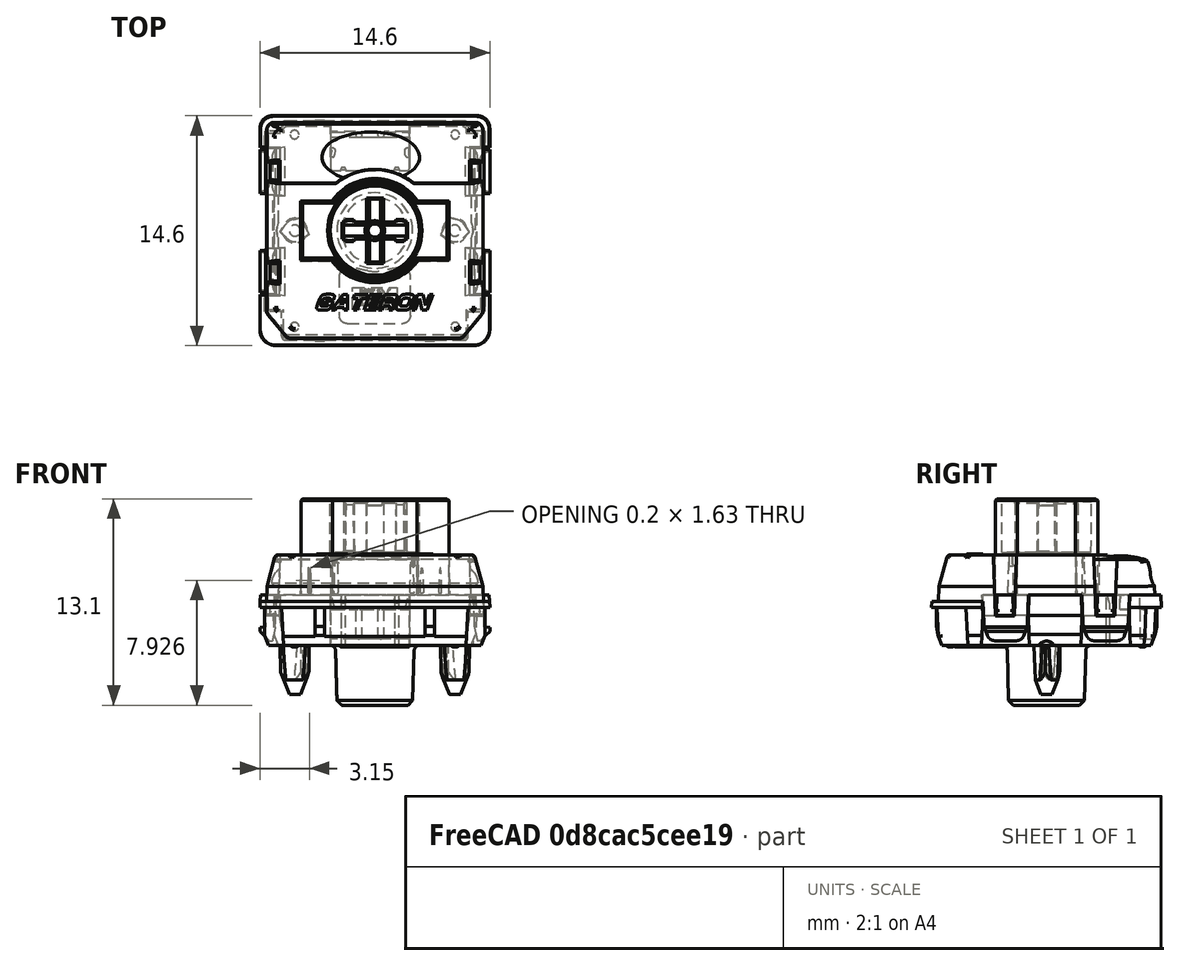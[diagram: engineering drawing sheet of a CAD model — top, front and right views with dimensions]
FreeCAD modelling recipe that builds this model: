
FCSTD DOCUMENT  (FreeCAD 1.0R39319 (Git))
Label: THT-HALL-SWITCH
License: All rights reserved
LicenseURL: https://en.wikipedia.org/wiki/All_rights_reserved
objects: PartDesign::CoordinateSystem×2, Part::Feature×1, PartDesign::FeatureBase×1, PartDesign::Body×1
note: 6 computed .brp shape members not serialized (recipe doc carries the construction recipe); baked Part::Feature solids carry a one-line shape summary decoded from their .brp

FEATURE [Part::Feature] Part__Feature  label="SOLID"
  Placement = pos=(13.3,-4.5,-1.1) rot=(0,0,1;0rad)
  shape: bbox 14.78 x 14.78 x 13.28 mm, 728 faces (baked)
FEATURE [PartDesign::CoordinateSystem] LCS_Origin
  AttacherType = Attacher::AttachEngine3D
  AttachmentOffset = pos=(-13.3,4.5,1.1) rot=(0,0,1;0rad)
  AttachmentSupport = -> [X_Axis]
  MapMode = 2
  Placement = pos=(-13.3,4.5,1.1) rot=(0,0,1;0rad)
FEATURE [PartDesign::FeatureBase] BaseFeature
  BaseFeature = -> Part__Feature
  Suppressed = false
FEATURE [PartDesign::CoordinateSystem] LCS_1
  AttacherType = Attacher::AttachEngine3D
  AttachmentSupport = -> [BaseFeature]
  MapMode = 11
  Placement = pos=(-13.3,4.5,8.00025) rot=(0.707107,0.707107,0;3.14159rad)
FEATURE [PartDesign::Body] Body
  AllowCompound = false
  BaseFeature = -> Part__Feature
  Group = -> [BaseFeature,LCS_Origin,LCS_1]
  Origin = -> Origin
  Tip = -> BaseFeature
